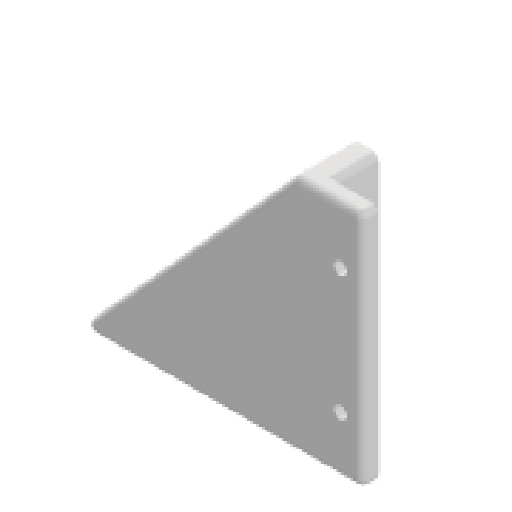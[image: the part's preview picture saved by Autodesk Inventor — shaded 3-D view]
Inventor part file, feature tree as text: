
AUTODESK INVENTOR PART (.ipt)
format: ipt  version: 2024.1 (Build 281209000, 209)  size: 292,352 bytes
history: native  units: mm
features: sketch x4, extrude x2, hole x2, projected_geometry x2, fillet x1
ambient origin geometry x8: Origin, YZ Plane, XZ Plane, XY Plane, X Axis, Y Axis, Z Axis, Center Point
bodies: Solid1 (feature_tree)
feature tree (11):
  extrude  "Extrusion1"  Depth=125.0mm
  extrude  "Extrusion2"  Depth=7.0mm TaperAngle=0.0deg
  fillet  "Fillet1"  Radius=20.0mm
  hole  "Hole1"  [1 undecoded]
  hole  "Hole3"  [1 undecoded]
  sketch  "Sketch1"  dims[d0=105.0mm d1=125.0mm]
  sketch  "Sketch2"  dims[d3=30.0mm d4=7.0mm d5=0.0mm d6=20.0mm]
  projected_geometry  "Projected Loop1"
  sketch  "Sketch3"  dims[d7=5.0mm d8=20.0mm d9=0.0mm]
  sketch  "Sketch5"  dims[d10=3.0mm d11=5.8mm d12=6.0mm d13=10.4mm d14=2.0mm d15=90.0deg d16=8.0mm d17=20.594885mm d18=25.0mm d19=10.0mm d23=55.0mm d31=5.8mm d32=6.0mm d33=4.0mm d34=2.0mm d35=90.0deg d36=8.0mm d37=20.594885mm d38=65.0mm d40=10.0mm]
  projected_geometry  "Projected Loop2"
note: 2 required parameter values undecoded (feature->parameter linkage not recoverable at this tier; creation-order binding heuristic only, values carry confidence <= 0.55)
